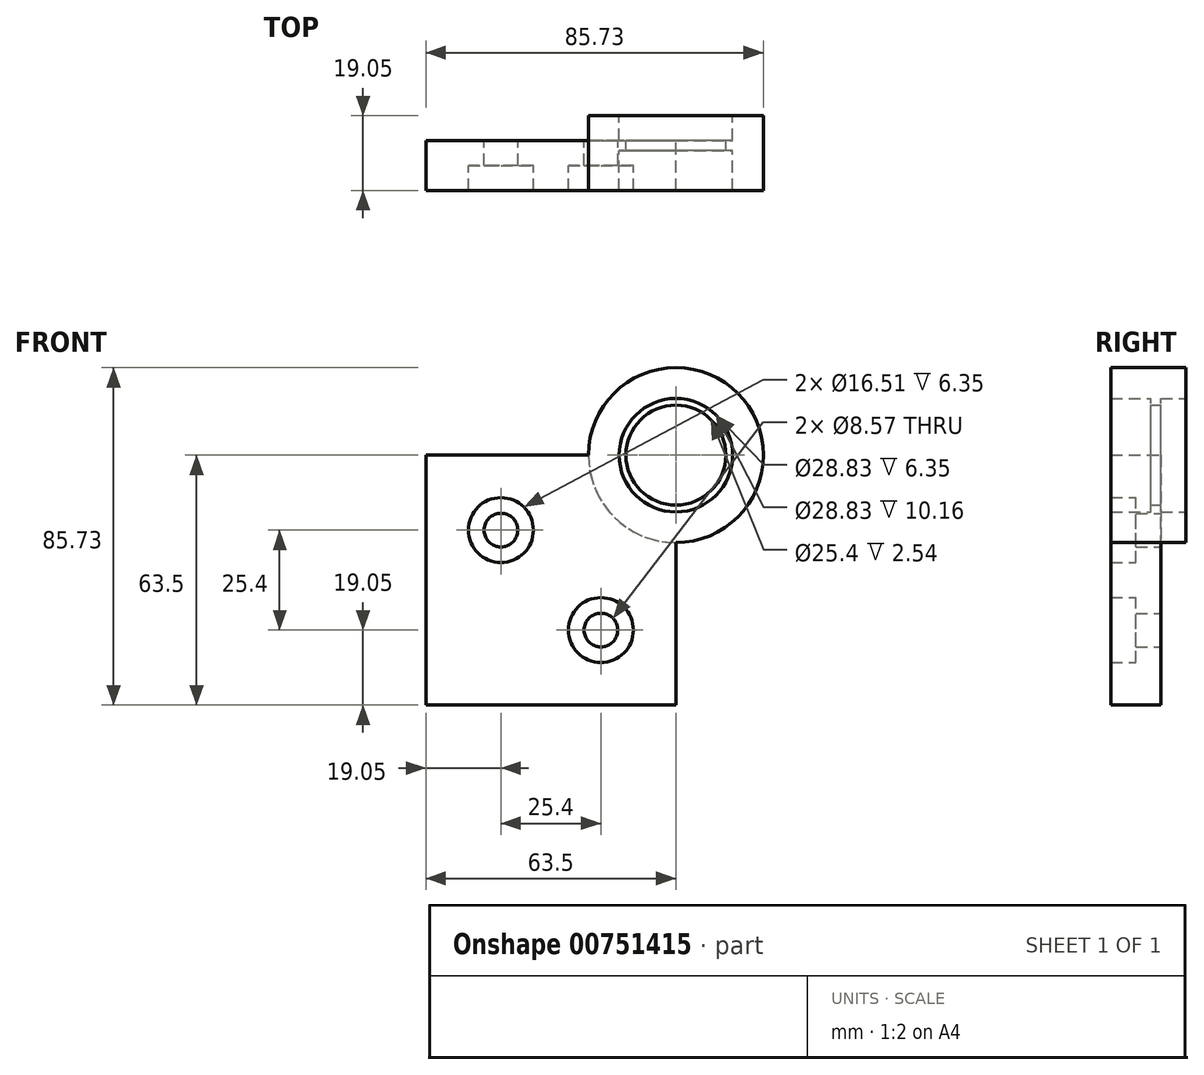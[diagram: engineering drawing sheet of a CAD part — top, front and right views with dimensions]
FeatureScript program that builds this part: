
annotation { "Feature Type Name" : "Feature", "Feature Type Description" : "" }
export const myFeature = defineFeature(function(context is Context, id is Id, definition is map)
    precondition{}
    {
        {
            var Q0;
            Q0=qCreatedBy(makeId("Front.planeOp"),FACE);
            var sketch = newSketch(context, id + "F0", { "sketchPlane" : qUnion([Q0])});
            skCircle(sketch, "E0", {"center": v(0, 0) * mm, "radius": 14.41 * mm});
            skCircle(sketch, "E1", {"center": v(0, 0) * mm, "radius": 12.7 * mm});
            skCircle(sketch, "E2", {"center": v(0, 0) * mm, "radius": 22.23 * mm});
            skLineSegment(sketch, "E3.bottom", {"start": v(0, 0) * mm, "end": v(-63.5, 0) * mm});
            skLineSegment(sketch, "E3.top", {"start": v(0, -63.5) * mm, "end": v(-63.5, -63.5) * mm});
            skLineSegment(sketch, "E3.left", {"start": v(0, 0) * mm, "end": v(0, -63.5) * mm});
            skLineSegment(sketch, "E3.right", {"start": v(-63.5, 0) * mm, "end": v(-63.5, -63.5) * mm});
            skCircle(sketch, "E4", {"center": v(-44.45, -19.05) * mm, "radius": 4.29 * mm});
            skCircle(sketch, "E5", {"center": v(-19.05, -44.45) * mm, "radius": 4.29 * mm});
            skCircle(sketch, "E6", {"center": v(-44.45, -19.05) * mm, "radius": 8.26 * mm});
            skCircle(sketch, "E7", {"center": v(-19.05, -44.45) * mm, "radius": 8.26 * mm});
            skSolve(sketch);
        }
        {
            var Q0;
            {var subQ0=sQuery(id+"F0.wireOp",EDGE,"E3.top");Q0=makeQuery(id+"F0.imprint","IMPRINT",FACE,{"disambiguationData":[TD([[makeQuery(id+"F0.imprint","IMPRINT",EDGE,{"derivedFrom":subQ0}),-1.0]])]});}
            extrude(context, id + "F1", {"entities" : qUnion([Q0]), "depth" : 12.7 * mm, "offsetDistance" : 25.4 * mm});
        }
        {
            var Q0;
            Q0=makeQuery(id+"F0.imprint","IMPRINT",FACE,{"disambiguationData":[TD([[makeQuery(id+"F0.imprint","IMPRINT",EDGE,{"derivedFrom":sQuery(id+"F0.wireOp",EDGE,"E4")}),-1.0]])]});
            var Q1;
            Q1=makeQuery(id+"F0.imprint","IMPRINT",FACE,{"disambiguationData":[TD([[makeQuery(id+"F0.imprint","IMPRINT",EDGE,{"derivedFrom":sQuery(id+"F0.wireOp",EDGE,"E5")}),-1.0]])]});
            extrude(context, id + "F2", {"entities" : qUnion([Q0, Q1]), "operationType" : NewBodyOperationType.ADD, "depth" : 6.35 * mm, "offsetDistance" : 25.4 * mm});
        }
        {
            var Q0;
            {var subQ0=sQuery(id+"F0.wireOp",EDGE,"E3.bottom");var subQ1=sQuery(id+"F0.wireOp",EDGE,"E0");var subQ2=makeQuery(id+"F0.imprint","INTERSECT",VERTEX,{"derivedFrom":[subQ1,subQ0]});Q0=makeQuery(id+"F0.imprint","IMPRINT",FACE,{"disambiguationData":[TD([[makeQuery(id+"F0.imprint","IMPRINT",EDGE,{"disambiguationData":[TD([[subQ2,-1.0]])],"derivedFrom":subQ1}),-1.0]])]});}
            var Q1;
            {var subQ0=sQuery(id+"F0.wireOp",EDGE,"E3.bottom");var subQ1=sQuery(id+"F0.wireOp",EDGE,"E0");var subQ2=makeQuery(id+"F0.imprint","INTERSECT",VERTEX,{"derivedFrom":[subQ1,subQ0]});Q1=makeQuery(id+"F0.imprint","IMPRINT",FACE,{"disambiguationData":[TD([[makeQuery(id+"F0.imprint","IMPRINT",EDGE,{"disambiguationData":[TD([[subQ2,1.0]])],"derivedFrom":subQ1}),-1.0]])]});}
            extrude(context, id + "F3", {"entities" : qUnion([Q0, Q1]), "operationType" : NewBodyOperationType.ADD, "depth" : 12.7 * mm, "offsetDistance" : 25.4 * mm, "hasSecondDirection" : true, "secondDirectionOppositeDirection" : true, "secondDirectionDepth" : 6.35 * mm});
        }
        {
            var Q0;
            {var subQ0=sQuery(id+"F0.wireOp",EDGE,"E3.bottom");var subQ1=sQuery(id+"F0.wireOp",EDGE,"E0");var subQ2=makeQuery(id+"F0.imprint","INTERSECT",VERTEX,{"derivedFrom":[subQ1,subQ0]});Q0=makeQuery(id+"F0.imprint","IMPRINT",FACE,{"disambiguationData":[TD([[makeQuery(id+"F0.imprint","IMPRINT",EDGE,{"disambiguationData":[TD([[subQ2,-1.0]])],"derivedFrom":subQ1}),1.0]])]});}
            var Q1;
            {var subQ0=sQuery(id+"F0.wireOp",EDGE,"E3.bottom");var subQ1=sQuery(id+"F0.wireOp",EDGE,"E0");var subQ2=makeQuery(id+"F0.imprint","INTERSECT",VERTEX,{"derivedFrom":[subQ1,subQ0]});Q1=makeQuery(id+"F0.imprint","IMPRINT",FACE,{"disambiguationData":[TD([[makeQuery(id+"F0.imprint","IMPRINT",EDGE,{"disambiguationData":[TD([[subQ2,1.0]])],"derivedFrom":subQ1}),1.0]])]});}
            extrude(context, id + "F4", {"entities" : qUnion([Q0, Q1]), "operationType" : NewBodyOperationType.ADD, "depth" : 2.54 * mm, "offsetDistance" : 25.4 * mm});
        }
    });
